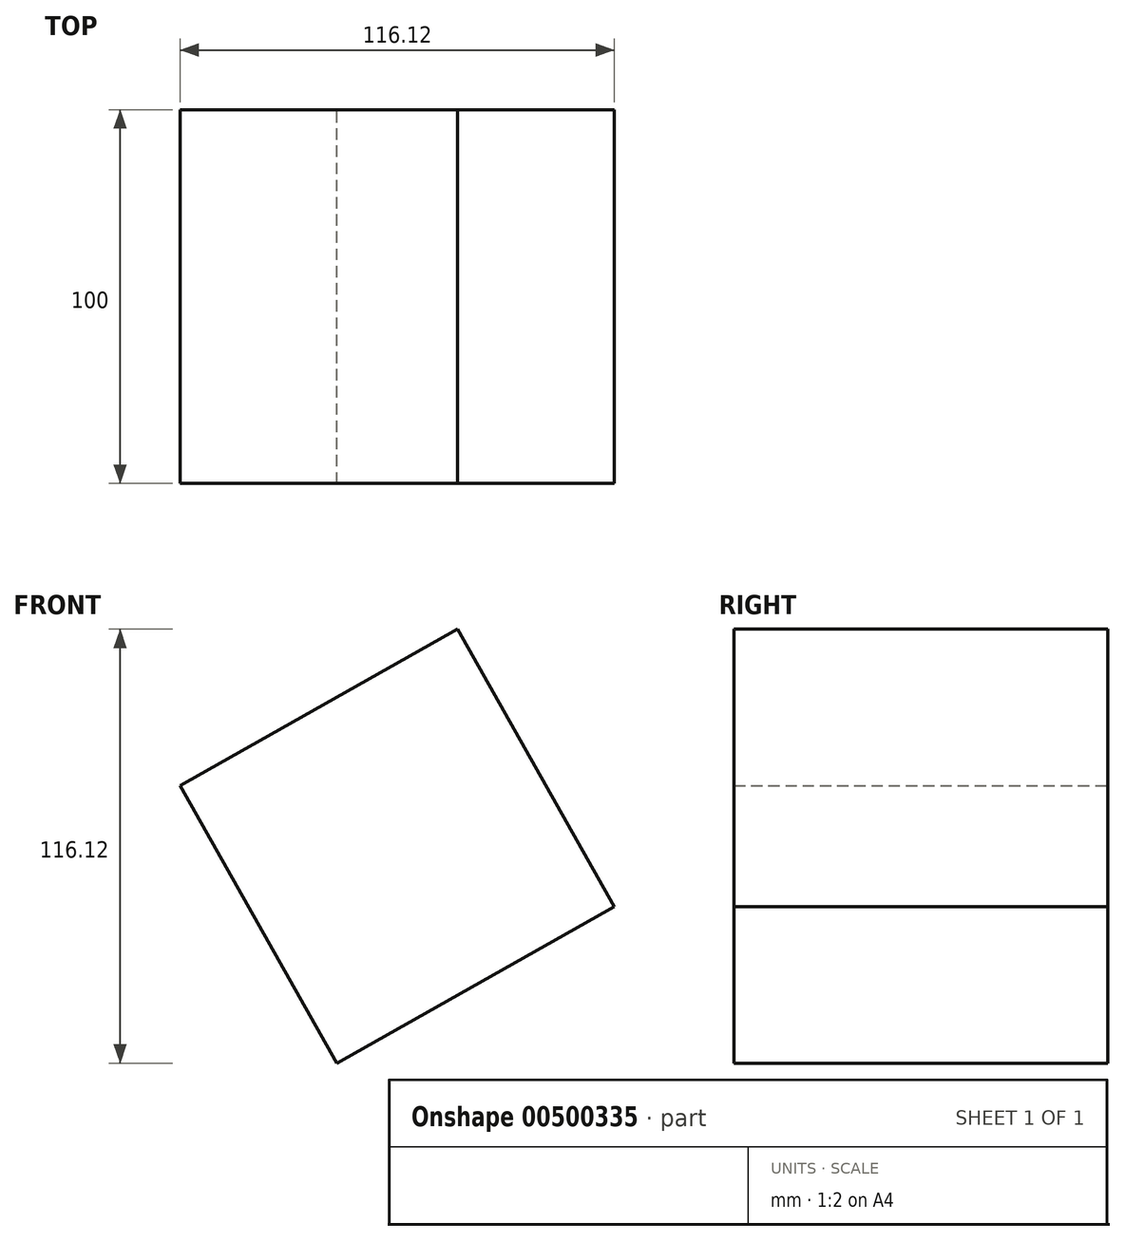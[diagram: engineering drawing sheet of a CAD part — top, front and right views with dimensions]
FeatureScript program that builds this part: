
annotation { "Feature Type Name" : "Feature", "Feature Type Description" : "" }
export const myFeature = defineFeature(function(context is Context, id is Id, definition is map)
    precondition{}
    {
        {
            var Q0;
            Q0=qCreatedBy(makeId("Front.planeOp"),FACE);
            var sketch = newSketch(context, id + "F0", { "sketchPlane" : qUnion([Q0])});
            skCircle(sketch, "E0.cCircle", {"center": v(0, 0) * mm, "radius": 60.27 * mm, "construction": true});
            skLineSegment(sketch, "E0.0", {"start": v(-16.15, -58.06) * mm, "end": v(-58.06, 16.15) * mm});
            skLineSegment(sketch, "E0.1", {"start": v(-58.06, 16.15) * mm, "end": v(16.15, 58.06) * mm});
            skLineSegment(sketch, "E0.2", {"start": v(16.15, 58.06) * mm, "end": v(58.06, -16.15) * mm});
            skLineSegment(sketch, "E0.3", {"start": v(58.06, -16.15) * mm, "end": v(-16.15, -58.06) * mm});
            skSolve(sketch);
        }
        {
            var Q0;
            Q0=makeQuery(id+"F0.imprint","IMPRINT",FACE,{"disambiguationData":[TD([[makeQuery(id+"F0.imprint","IMPRINT",EDGE,{"derivedFrom":sQuery(id+"F0.wireOp",EDGE,"E0.0")}),-1.0]])]});
            extrude(context, id + "F1", {"entities" : qUnion([Q0]), "depth" : 100 * mm});
        }
    });
